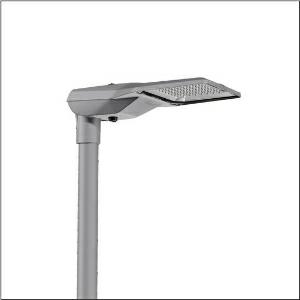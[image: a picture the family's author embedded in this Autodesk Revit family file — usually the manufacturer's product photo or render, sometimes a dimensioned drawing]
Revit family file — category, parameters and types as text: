
# Revit family: streetlight_sl_21_midi___st1_0a_5xe3d43t08mb_aa37
name_source: partatom
category: Lighting Fixtures
units: mm (PartAtom-declared; Revit-internal decimal feet)

## family parameters
Cut with Voids When Loaded = No
Host = Face
Light Source = No
Part Type = Normal
Room Calculation Point = No
Round Connector Dimension = Use Diameter
Shared = No

## types (1)
- --- (1 x LED, 20180 lm, 147 W, 4000K)
    Apparent Load = 147 VA
    CIE Flux Codes = 37 72 97 100 100
    Color Rendering = 70
    Color Temperature = 4000K
    Default Elevation = 1800 mm
    Description = Streetlight SL 21 midi, mast luminaire, primary light control with lens, of PMMA, primary optical cover: cover, of toughened safety glass, transparent, light distribution: ST1.0a, light emission: direct distribution, primary light characteristic: asymmetric, installation type: side-entry, post-top, LED, High Power LED, rated luminous flux: 20.180lm, luminous efficacy: 137lm/W, light colour: 740, colour temperature: 4000K, control gear: D4i, control: overheat protection, constant luminous flux control, time-dependent luminous flux control, flexible luminous flux parameterisation, pre-setting: logarithmic dimming characteristic, mains connection: 230..240V, AC, 50/60Hz, start of lifetime: 147W, end of service life: 155W, reduction: 65W, luminaire housing, of diecast aluminium, powder-coated, Siteco® metallic grey (DB 702S), corrosivity category C5 mid according to DIN EN ISO 12944, please order mast flange separately, inclination adjustable: 0°, 5°, 10°, 15°, sealing non-destructively replaceable, multi-level sealing system, length: 644mm, width: 335mm, height: 110mm, mast flange for spigot size: 42mm (side-entry): 5XC10008XM4, 60/48mm (side-entry/post-top): 5XC10108XM2, 76/60mm (side-entry/post-top): 5XC10108XM1, mounting height: 4..8m, Smart Interface below and above, protection rating (complete): IP66, insulation class (complete): insulation class II (safety insulation), certification: CE, ENEC, ENEC+, VDE, impact resistance: IK10, permissible operating ambient temperature for outdoor applications: -40..+50°C, standard-compliant lighting for roads and squares, packaging unit: 1 piece

Light Distribution: ST1.0a
    Height = 111 mm
    Lamp = 1 x LED
    Lamp Light Flux = 20180 lm
    Lamp Power = 147 W
    Lamp count = 1
    Length = 644 mm
    Luminous efficacy = 137 lm/W
    Manufacturer = Siteco
    ModVariant = No
    Model = 5XE3D43T08MB
    Number of Poles = 1
    OnlyDefault = Yes
    Power Factor = 1
    Product Name = Streetlight SL 21 midi | ST1.0a
    Product group = mast luminaire | pylon top
    ProductGroupID = 6100
    Protection Class = Protection class II
    Protection Degree = IP 66
    RLX_Detail_Level = 1
    RLX_Emergency_Light_Flux = 0 lm
    RLX_Emergency_Type = 0
    RLX_Emergency_Type_DB = No
    RlxData = <blob elided: 26937 chars, md5=e0cad18c>
    Socket = socket
    Standby Power = 0 W
    System Light Flux = 20180 lm
    System Power = 147 W
    Type Comments = factory setting: luminous flux: 100 % | dim-lin: 254 | 750 mA
    Type Image = l_1004304.jpg
    URL = http://relux.com
    VarID = @adj_210529
    Voltage = 0 V
    Weight = 0.00 kg
    Width = 336 mm

## geometry (parser evidence)
native form markers: Blend x4, Sweep x11
no freeform markers — native parametric forms only
